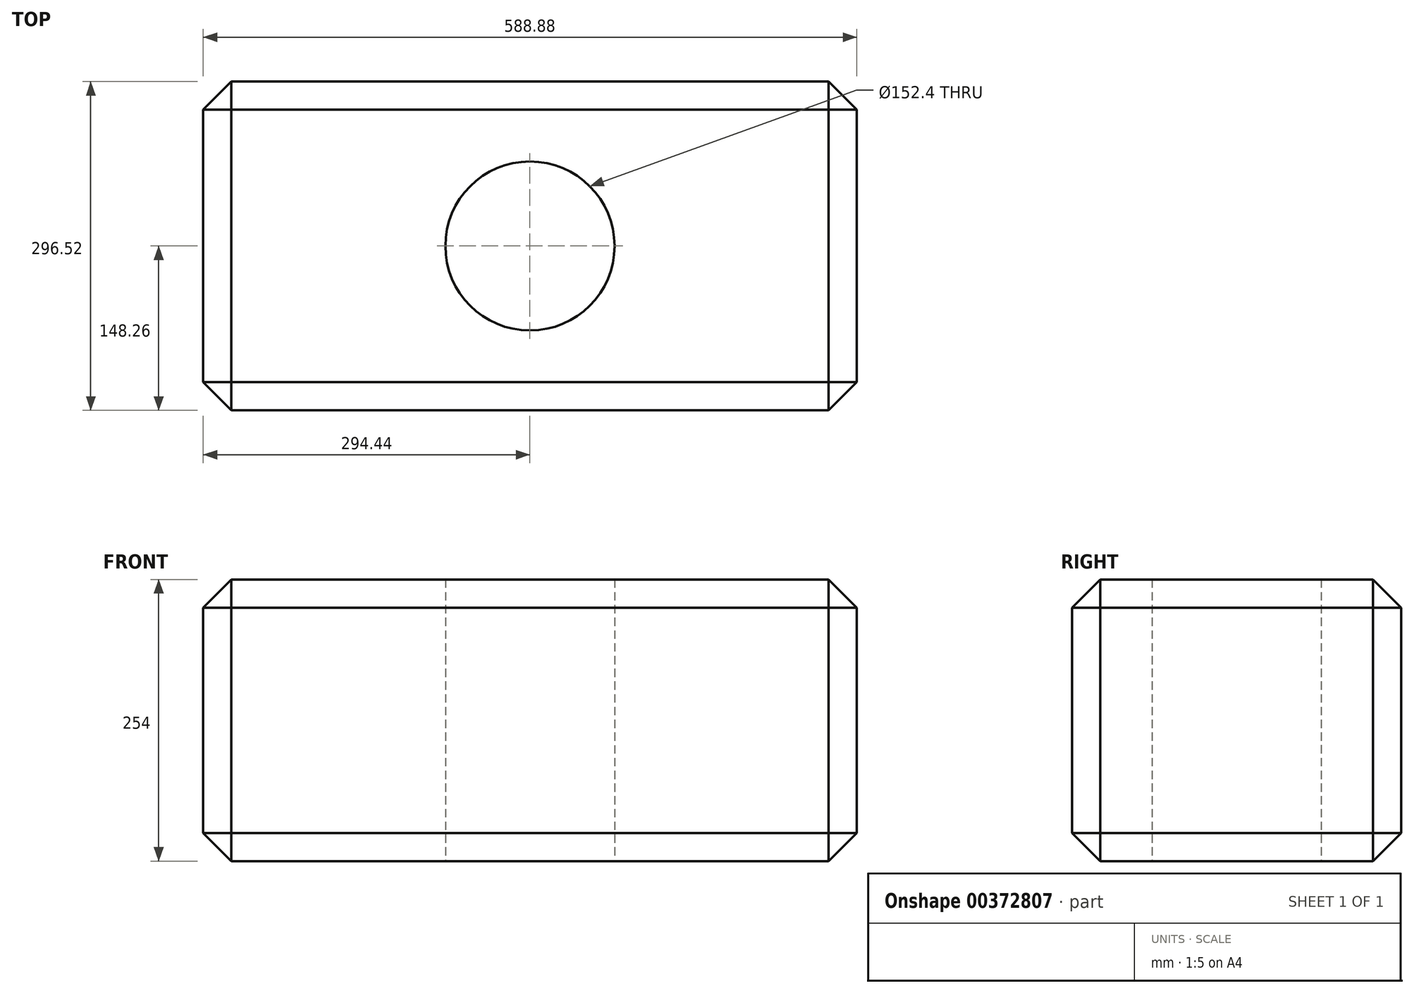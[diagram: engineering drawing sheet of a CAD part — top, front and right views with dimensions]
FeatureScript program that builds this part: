
annotation { "Feature Type Name" : "Feature", "Feature Type Description" : "" }
export const myFeature = defineFeature(function(context is Context, id is Id, definition is map)
    precondition{}
    {
        {
            var Q0;
            Q0=qCreatedBy(makeId("Top.planeOp"),FACE);
            var sketch = newSketch(context, id + "F0", { "sketchPlane" : qUnion([Q0])});
            skLineSegment(sketch, "E0.bottom", {"start": v(294.44, 148.26) * mm, "end": v(-294.44, 148.26) * mm});
            skLineSegment(sketch, "E0.top", {"start": v(294.44, -148.26) * mm, "end": v(-294.44, -148.26) * mm});
            skLineSegment(sketch, "E0.left", {"start": v(294.44, 148.26) * mm, "end": v(294.44, -148.26) * mm});
            skLineSegment(sketch, "E0.right", {"start": v(-294.44, 148.26) * mm, "end": v(-294.44, -148.26) * mm});
            skPoint(sketch, "E0.middle", {"position": v(0, 0) * mm});
            skCircle(sketch, "E1", {"center": v(0, 0) * mm, "radius": 76.2 * mm});
            skSolve(sketch);
        }
        {
            var Q0;
            Q0=makeQuery(id+"F0.imprint","IMPRINT",FACE,{"disambiguationData":[TD([[makeQuery(id+"F0.imprint","IMPRINT",EDGE,{"derivedFrom":sQuery(id+"F0.wireOp",EDGE,"E0.bottom")}),1.0]])]});
            extrude(context, id + "F1", {"entities" : qUnion([Q0]), "depth" : 254 * mm});
        }
        {
            var Q0;
            Q0=makeQuery(id+"F1.opExtrude","CAP_EDGE",EDGE,{"disambiguationData":[OSD([sQuery(id+"F0.wireOp",EDGE,"E0.top")])],"isStart":false});
            var Q1;
            Q1=makeQuery(id+"F1.opExtrude","CAP_EDGE",EDGE,{"disambiguationData":[OSD([sQuery(id+"F0.wireOp",EDGE,"E0.left")])],"isStart":false});
            var Q2;
            Q2=makeQuery(id+"F1.opExtrude","CAP_EDGE",EDGE,{"disambiguationData":[OSD([sQuery(id+"F0.wireOp",EDGE,"E0.bottom")])],"isStart":false});
            var Q3;
            Q3=makeQuery(id+"F1.opExtrude","CAP_EDGE",EDGE,{"disambiguationData":[OSD([sQuery(id+"F0.wireOp",EDGE,"E0.right")])],"isStart":false});
            var Q4;
            Q4=makeQuery(id+"F1.opExtrude","SWEPT_EDGE",EDGE,{"disambiguationData":[OSD([sQuery(id+"F0.wireOp",EDGE,"E0.bottom"),sQuery(id+"F0.wireOp",EDGE,"E0.left")])]});
            var Q5;
            Q5=makeQuery(id+"F1.opExtrude","SWEPT_EDGE",EDGE,{"disambiguationData":[OSD([sQuery(id+"F0.wireOp",EDGE,"E0.top"),sQuery(id+"F0.wireOp",EDGE,"E0.left")])]});
            var Q6;
            Q6=makeQuery(id+"F1.opExtrude","SWEPT_EDGE",EDGE,{"disambiguationData":[OSD([sQuery(id+"F0.wireOp",EDGE,"E0.top"),sQuery(id+"F0.wireOp",EDGE,"E0.right")])]});
            var Q7;
            Q7=makeQuery(id+"F1.opExtrude","SWEPT_EDGE",EDGE,{"disambiguationData":[OSD([sQuery(id+"F0.wireOp",EDGE,"E0.bottom"),sQuery(id+"F0.wireOp",EDGE,"E0.right")])]});
            var Q8;
            Q8=makeQuery(id+"F1.opExtrude","CAP_EDGE",EDGE,{"disambiguationData":[OSD([sQuery(id+"F0.wireOp",EDGE,"E0.bottom")])],"isStart":true});
            var Q9;
            Q9=makeQuery(id+"F1.opExtrude","CAP_EDGE",EDGE,{"disambiguationData":[OSD([sQuery(id+"F0.wireOp",EDGE,"E0.left")])],"isStart":true});
            var Q10;
            Q10=makeQuery(id+"F1.opExtrude","CAP_EDGE",EDGE,{"disambiguationData":[OSD([sQuery(id+"F0.wireOp",EDGE,"E0.top")])],"isStart":true});
            var Q11;
            Q11=makeQuery(id+"F1.opExtrude","CAP_EDGE",EDGE,{"disambiguationData":[OSD([sQuery(id+"F0.wireOp",EDGE,"E0.right")])],"isStart":true});
            chamfer(context, id + "F2", {"entities" : qUnion([Q0, Q1, Q2, Q3, Q4, Q5, Q6, Q7, Q8, Q9, Q10, Q11]), "width" : 25.4 * mm, "tangentPropagation" : true});
        }
    });
